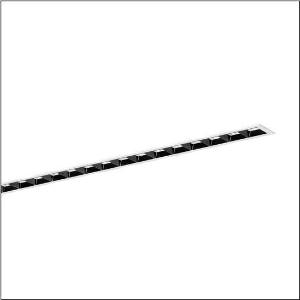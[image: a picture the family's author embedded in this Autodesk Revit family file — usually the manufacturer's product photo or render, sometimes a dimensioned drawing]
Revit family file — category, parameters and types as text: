
# Revit family: silica_21_51mx11tat4w
name_source: partatom
category: Lighting Fixtures
units: mm (PartAtom-declared; Revit-internal decimal feet)

## family parameters
Cut with Voids When Loaded = No
Host = Face
Light Source = No
Part Type = Normal
Room Calculation Point = No
Round Connector Dimension = Use Diameter
Shared = No

## types (1)
- --- (1 x LED, 3720 lm, 32.2 W, 6500K)
    Apparent Load = 32 VA
    CIE Flux Codes = 85 99 100 100 100
    Color Rendering = 80
    Color Temperature = 6500K
    Default Elevation = 1800 mm
    Description = Silica 21, office luminaire, primary light control with darklight reflector, of PMMA, black, CAT 2 (L<= 3000cd/m²), light emission: direct distribution, primary light characteristic: symmetric, installation type: recessed, LED, rated luminous flux: 3.720lm, luminous efficacy: 110lm/W, light colour: 8tw, colour temperature: 2700..6500K, control gear: DALI DT8, with terminal, 3+2-pole, max. 2.5mm², mains connection: 220..240V, AC, 50/60Hz, rated input power: 33.8W, luminaire housing, of aluminium, traffic white (RAL 9016), length: 1.228mm, width: 79mm, height: 53mm, protection rating (complete): IP20, insulation class (complete): insulation class I (protective earthing), certification: CE, ENEC, VDE, permissible operating ambient temperature: 0..+35°C, standard: EN 50419, packaging unit: 1 piece
    Height = 0 mm  [stored 0 ft]
    Lamp = 1 x LED
    Lamp Light Flux = 3720 lm
    Lamp Power = 32.2 W
    Lamp count = 1
    Length = 1227 mm
    Luminous efficacy = 116 lm/W
    Manufacturer = Siteco
    ModVariant = No
    Model = 51MX11TAT4W
    Mounting Place = Ceiling
    Mounting Type = Recessed
    Number of Poles = 1
    OnlyDefault = Yes
    Power Factor = 1
    Product Name = Silica 21
    Product group = office luminaire | ceiling recessed
    ProductGroupID = 400
    Protection Class = Protection class I
    Protection Degree = IP 20
    RLX_Detail_Level = 1
    RLX_Emergency_Light_Flux = 0 lm
    RLX_Emergency_Type = 0
    RLX_Emergency_Type_DB = No
    RlxData = <blob elided: 35825 chars, md5=dd06ec6f>
    Socket = socket
    Standby Power = 0 W
    System Light Flux = 3720 lm
    System Power = 32 W
    Type Comments = individual setting
    Type Image = l_1335880.jpg
    URL = http://relux.com
    VarID = @adj_141157
    Voltage = 0 V
    Weight = 0.00 kg
    Width = 79 mm

note: [stored X ft] marks values corroborated as IEEE doubles in the binary element streams (Revit-internal decimal feet)

## geometry (parser evidence)
native form markers: Blend x4, Sweep x9
no freeform markers — native parametric forms only
